# Revit family: Plumbing_Fixture-Grohe-Euroeco_Special-Wash_safety_basin_mixer_0.5inch-12-METRIC
name_source: partatom
category: Plumbing Fixtures
revit_build: Autodesk Revit Architecture 2012 (Build: 20110916_2132(x64)
units: mm (PartAtom-declared; Revit-internal decimal feet)

## types (1)
- Euroeco Safety Mixer 32 790 000
    ADA Compliant = Yes
    Assembly Code = C1030220
    AssetType = Fixed
    Barcode = 0
    CW Connection = Yes
    CWFU = 4.5
    Cold Water Connection Diameter = 10 mm  [stored 0.0328084 ft]
    Cold Water Radius = 5 mm  [stored 0.0164042 ft]
    Cost = 0 $
    Default Elevation = 600 mm
    Description = Washing your hands with your hands free – this is the idea behind the wall-mounted Euroeco mixers. Wall-mounted installation keeps the basin free, and in order to reduce the risk of accidents caused by projecting parts, faucet levers and spouts are available in a choice of lengths.
    Ecojoy = No
    ExpectedLife = 0
    Flow Pressure = min 0.5 bar/recommended 1 - 5 bar
    Flow Rate = approx 8 L/min
    HW Connection = Yes
    HWFU = 4.5
    Height = 226 mm
    Hot Water Connection Diameter = 10 mm  [stored 0.0328084 ft]
    Hot Water Radius = 5 mm  [stored 0.0164042 ft]
    Keynote = N13
    Length = 129 mm
    Low Emitting Material = No
    MaintenanceInformation = http://cdn08.grohe.com
    Manufacturer = Grohe AG
    Material = Grohe-Chrome
    Mixing Leaver = Yes
    Model = Euroeco Safety Mixer 32 790 000
    ModelNumber = Euroeco Safety Mixer 32 790 000
    Name = Euroeco Safety Mixer 32 790 000
    Operating Pressure = max 10 bar
    Percentage of Recycled Content = 0
    Product Documentation Link = http://cdn08.grohe.com
    Product Page URL = http://www.grohe.com
    SerialNumber = 0
    Spare Parts List = http://www.grohe.com
    SpareParts = Lever 120 mm (46686 000), Temperature limiter (46277 000), Cartridge (46278 000), Flow straightener (13960 000), Shank fastening assembly (46249 000)
    TagNumber = 0
    Temp - Hot Water Supply = max 80°C
    Temp - Hot Water Supply (Recommended) = 60°C
    Test Pressure = 16 bar
    Type Comments = Single-lever safety basin mixer 1/2"
    URL = www.grohe.com
    Vent Connection = No
    WFU = 0
    Waste Connection = No
    Width = 0 mm  [stored 0 ft]
    _BIMspec_GUID = 0
    _current revision = 1
    _distributed by = www.bimstore.co.uk

note: [stored X ft] marks values corroborated as IEEE doubles in the binary element streams (Revit-internal decimal feet)

## geometry (parser evidence)
native form markers: Blend x4, Sweep x6
no freeform markers — native parametric forms only
